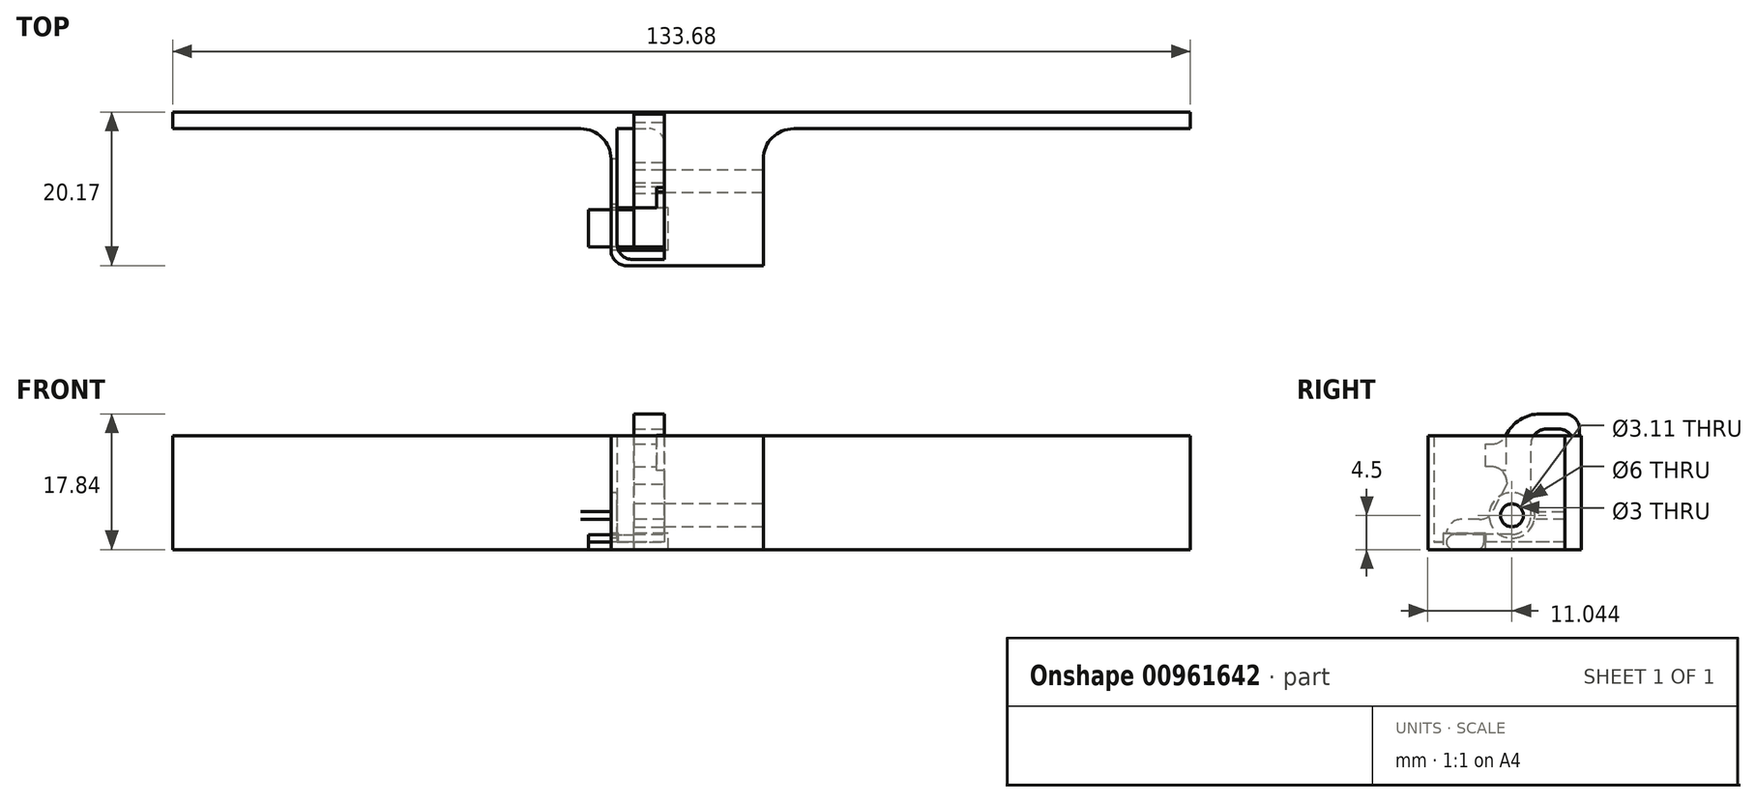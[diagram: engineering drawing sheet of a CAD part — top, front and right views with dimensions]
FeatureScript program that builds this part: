
annotation { "Feature Type Name" : "Feature", "Feature Type Description" : "" }
export const myFeature = defineFeature(function(context is Context, id is Id, definition is map)
    precondition{}
    {
        {
            var Q0;
            Q0=qCreatedBy(makeId("Top.planeOp"),FACE);
            var sketch = newSketch(context, id + "F0", { "sketchPlane" : qUnion([Q0])});
            skLineSegment(sketch, "E0.bottom", {"start": v(-38.38, 26.4) * mm, "end": v(95.3, 26.4) * mm});
            skLineSegment(sketch, "E0.top", {"start": v(-38.38, 24.23) * mm, "end": v(95.3, 24.23) * mm});
            skLineSegment(sketch, "E0.left", {"start": v(-38.38, 26.4) * mm, "end": v(-38.38, 24.23) * mm});
            skLineSegment(sketch, "E0.right", {"start": v(95.3, 26.4) * mm, "end": v(95.3, 24.23) * mm});
            skLineSegment(sketch, "E1.bottom", {"start": v(26.2, 24.23) * mm, "end": v(39.2, 24.23) * mm});
            skLineSegment(sketch, "E1.top", {"start": v(26.2, 6.23) * mm, "end": v(39.2, 6.23) * mm});
            skLineSegment(sketch, "E1.left", {"start": v(26.2, 24.23) * mm, "end": v(26.2, 6.23) * mm});
            skLineSegment(sketch, "E1.right", {"start": v(39.2, 24.23) * mm, "end": v(39.2, 6.23) * mm});
            skSolve(sketch);
        }
        {
            var Q0;
            Q0 = qSketchRegion(id + "F0", true);
            extrude(context, id + "F1", {"entities" : qUnion([Q0]), "depth" : 15 * mm, "offsetDistance" : 25 * mm});
        }
        {
            var Q0;
            Q0=makeQuery(id+"F1.opExtrude","CAP_FACE",FACE,{"disambiguationData":[OSD([sQuery(id+"F0.wireOp",EDGE,"E0.bottom"),sQuery(id+"F0.wireOp",EDGE,"E0.top"),sQuery(id+"F0.wireOp",EDGE,"E0.left"),sQuery(id+"F0.wireOp",EDGE,"E0.right"),sQuery(id+"F0.wireOp",EDGE,"E1.top"),sQuery(id+"F0.wireOp",EDGE,"E1.left"),sQuery(id+"F0.wireOp",EDGE,"E1.right")])],"isStart":true});
            var sketch = newSketch(context, id + "F2", { "sketchPlane" : qUnion([Q0])});
            skLineSegment(sketch, "E2.bottom", {"start": v(26.2, -6.23) * mm, "end": v(19.2, -6.23) * mm});
            skLineSegment(sketch, "E2.top", {"start": v(26.2, -25.17) * mm, "end": v(19.2, -25.17) * mm});
            skLineSegment(sketch, "E2.left", {"start": v(26.2, -6.23) * mm, "end": v(26.2, -25.17) * mm});
            skLineSegment(sketch, "E2.right", {"start": v(19.2, -6.23) * mm, "end": v(19.2, -25.17) * mm});
            skSolve(sketch);
        }
        {
            var Q0;
            {var subQ0=sQuery(id+"F2.wireOp",EDGE,"E2.bottom");Q0=makeQuery(id+"F2.imprint","IMPRINT",FACE,{"disambiguationData":[TD([[makeQuery(id+"F2.imprint","IMPRINT",EDGE,{"derivedFrom":subQ0}),1.0]])]});}
            extrude(context, id + "F3", {"entities" : qUnion([Q0]), "operationType" : NewBodyOperationType.ADD, "oppositeDirection" : true, "depth" : 1 * mm, "offsetDistance" : 25 * mm});
        }
        {
            var Q0;
            Q0=makeQuery(id+"F3.opExtrude","CAP_FACE",FACE,{"disambiguationData":[OSD([sQuery(id+"F0.wireOp",EDGE,"E0.top"),sQuery(id+"F2.wireOp",EDGE,"E2.bottom"),sQuery(id+"F2.wireOp",EDGE,"E2.left"),sQuery(id+"F2.wireOp",EDGE,"E2.right")])],"isStart":false});
            var sketch = newSketch(context, id + "F4", { "sketchPlane" : qUnion([Q0])});
            skLineSegment(sketch, "E3.bottom", {"start": v(19.2, 24.23) * mm, "end": v(20, 24.23) * mm});
            skLineSegment(sketch, "E3.top", {"start": v(19.2, 6.23) * mm, "end": v(20, 6.23) * mm});
            skLineSegment(sketch, "E3.left", {"start": v(19.2, 24.23) * mm, "end": v(19.2, 6.23) * mm});
            skLineSegment(sketch, "E3.right", {"start": v(20, 24.23) * mm, "end": v(20, 6.23) * mm});
            skLineSegment(sketch, "E4.bottom", {"start": v(20, 6.23) * mm, "end": v(26.2, 6.23) * mm});
            skLineSegment(sketch, "E4.top", {"start": v(20, 7.03) * mm, "end": v(26.2, 7.03) * mm});
            skLineSegment(sketch, "E4.left", {"start": v(20, 6.23) * mm, "end": v(20, 7.03) * mm});
            skLineSegment(sketch, "E4.right", {"start": v(26.2, 6.23) * mm, "end": v(26.2, 7.03) * mm});
            skSolve(sketch);
        }
        {
            var Q0;
            Q0=makeQuery(id+"F4.imprint","IMPRINT",FACE,{"disambiguationData":[TD([[makeQuery(id+"F4.imprint","IMPRINT",EDGE,{"derivedFrom":sQuery(id+"F4.wireOp",EDGE,"E3.bottom")}),-1.0]])]});
            var Q1;
            Q1=makeQuery(id+"F4.imprint","IMPRINT",FACE,{"disambiguationData":[TD([[makeQuery(id+"F4.imprint","IMPRINT",EDGE,{"derivedFrom":sQuery(id+"F4.wireOp",EDGE,"E4.bottom")}),-1.0]])]});
            extrude(context, id + "F5", {"entities" : qUnion([Q0, Q1]), "operationType" : NewBodyOperationType.ADD, "depth" : 14 * mm, "offsetDistance" : 25 * mm});
        }
        {
            var Q0;
            Q0=makeQuery(id+"F5.boolean.opBoolean","MERGE",EDGE,{"derivedFrom":[makeQuery(id+"F3.opExtrude","SWEPT_EDGE",EDGE,{"disambiguationData":[OSD([sQuery(id+"F2.wireOp",EDGE,"E2.bottom"),sQuery(id+"F2.wireOp",EDGE,"E2.right")])]}),makeQuery(id+"F5.opExtrude","SWEPT_EDGE",EDGE,{"disambiguationData":[OSD([sQuery(id+"F4.wireOp",EDGE,"E3.top"),sQuery(id+"F4.wireOp",EDGE,"E3.left")])]})]});
            var Q1;
            Q1=makeQuery(id+"F1.opExtrude","SWEPT_EDGE",EDGE,{"disambiguationData":[OSD([sQuery(id+"F0.wireOp",EDGE,"E0.top"),sQuery(id+"F0.wireOp",EDGE,"E1.bottom"),sQuery(id+"F0.wireOp",EDGE,"E1.left")])]});
            var Q2;
            Q2=makeQuery(id+"F5.opExtrude","SWEPT_EDGE",EDGE,{"disambiguationData":[OSD([sQuery(id+"F0.wireOp",EDGE,"E0.top"),sQuery(id+"F4.wireOp",EDGE,"E3.bottom"),sQuery(id+"F4.wireOp",EDGE,"E3.right")])]});
            var Q3;
            Q3=makeQuery(id+"F5.opExtrude","SWEPT_EDGE",EDGE,{"disambiguationData":[OSD([sQuery(id+"F4.wireOp",EDGE,"E3.right"),sQuery(id+"F4.wireOp",EDGE,"E4.top"),sQuery(id+"F4.wireOp",EDGE,"E4.left")])]});
            var Q4;
            Q4=makeQuery(id+"F5.opExtrude","SWEPT_EDGE",EDGE,{"disambiguationData":[OSD([sQuery(id+"F2.wireOp",EDGE,"E2.left"),sQuery(id+"F4.wireOp",EDGE,"E4.top"),sQuery(id+"F4.wireOp",EDGE,"E4.right")])]});
            fillet(context, id + "F6", {"entities" : qUnion([Q0, Q1, Q2, Q3, Q4]), "radius" : 2 * mm, "tangentPropagation" : true, "allowEdgeOverflow" : false});
        }
        {
            var Q0;
            Q0=makeQuery(id+"F5.boolean.opBoolean","MERGE",FACE,{"derivedFrom":[makeQuery(id+"F3.opExtrude","SWEPT_FACE",FACE,{"disambiguationData":[OSD([sQuery(id+"F2.wireOp",EDGE,"E2.right")])]}),makeQuery(id+"F5.opExtrude","SWEPT_FACE",FACE,{"disambiguationData":[OSD([sQuery(id+"F4.wireOp",EDGE,"E3.left")])]})]});
            var sketch = newSketch(context, id + "F7", { "sketchPlane" : qUnion([Q0])});
            skCircle(sketch, "E5", {"center": v(-17.27, 4.5) * mm, "radius": 3 * mm});
            skSolve(sketch);
        }
        {
            var Q0;
            Q0 = qSketchRegion(id + "F7", true);
            extrude(context, id + "F8", {"entities" : qUnion([Q0]), "operationType" : NewBodyOperationType.REMOVE, "oppositeDirection" : true, "depth" : 2 * mm, "offsetDistance" : 25 * mm});
        }
        {
            var Q0;
            Q0=makeQuery(id+"F1.opExtrude","SWEPT_FACE",FACE,{"disambiguationData":[OSD([sQuery(id+"F0.wireOp",EDGE,"E1.left")])]});
            var sketch = newSketch(context, id + "F9", { "sketchPlane" : qUnion([Q0])});
            skCircle(sketch, "E6", {"center": v(-17.27, 4.5) * mm, "radius": 1.5 * mm});
            skSolve(sketch);
        }
        {
            var Q0;
            Q0 = qSketchRegion(id + "F9", true);
            extrude(context, id + "F10", {"entities" : qUnion([Q0]), "operationType" : NewBodyOperationType.REMOVE, "oppositeDirection" : true, "depth" : 25 * mm, "offsetDistance" : 25 * mm});
        }
        {
            var Q0;
            Q0=makeQuery(id+"F1.opExtrude","SWEPT_EDGE",EDGE,{"disambiguationData":[OSD([sQuery(id+"F0.wireOp",EDGE,"E0.top"),sQuery(id+"F0.wireOp",EDGE,"E1.bottom"),sQuery(id+"F0.wireOp",EDGE,"E1.right")])]});
            var Q1;
            Q1=makeQuery(id+"F5.boolean.opBoolean","MERGE",EDGE,{"derivedFrom":[makeQuery(id+"F3.opExtrude","SWEPT_EDGE",EDGE,{"disambiguationData":[OSD([sQuery(id+"F0.wireOp",EDGE,"E0.top"),sQuery(id+"F2.wireOp",EDGE,"E2.right")])]}),makeQuery(id+"F5.opExtrude","SWEPT_EDGE",EDGE,{"disambiguationData":[OSD([sQuery(id+"F4.wireOp",EDGE,"E3.bottom"),sQuery(id+"F4.wireOp",EDGE,"E3.left")])]})]});
            fillet(context, id + "F11", {"entities" : qUnion([Q0, Q1]), "radius" : 4 * mm, "tangentPropagation" : true, "allowEdgeOverflow" : false});
        }
        {
            var Q0;
            Q0=makeQuery(id+"F1.opExtrude","SWEPT_FACE",FACE,{"disambiguationData":[OSD([sQuery(id+"F0.wireOp",EDGE,"E1.left")])]});
            var sketch = newSketch(context, id + "F12", { "sketchPlane" : qUnion([Q0])});
            skCircle(sketch, "E7", {"center": v(-17.27, 4.5) * mm, "radius": 1.55 * mm});
            skArc(sketch, "E8", {"start": v(-14.83, 3.98) * mm, "mid": v(-14.8, 4.83) * mm, "end": v(-15.05, 5.65) * mm});
            skLineSegment(sketch, "E9", {"start": v(-19.77, 4.52) * mm, "end": v(-19.77, 15.84) * mm});
            skLineSegment(sketch, "E10", {"start": v(-19.77, 15.84) * mm, "end": v(-25.1, 15.84) * mm});
            skLineSegment(sketch, "E11", {"start": v(-25.1, 15.84) * mm, "end": v(-25.1, 15) * mm});
            skLineSegment(sketch, "E12", {"start": v(-25.1, 15) * mm, "end": v(-26.15, 15) * mm});
            skLineSegment(sketch, "E13", {"start": v(-26.15, 15) * mm, "end": v(-26.15, 17.84) * mm});
            skLineSegment(sketch, "E14", {"start": v(-26.15, 17.84) * mm, "end": v(-16.7, 17.84) * mm});
            skLineSegment(sketch, "E15", {"start": v(-16.7, 17.84) * mm, "end": v(-16.7, 13.9) * mm});
            skLineSegment(sketch, "E16", {"start": v(-16.7, 13.9) * mm, "end": v(-13.85, 13.9) * mm});
            skLineSegment(sketch, "E17", {"start": v(-13.85, 13.9) * mm, "end": v(-13.85, 10.9) * mm});
            skLineSegment(sketch, "E18", {"start": v(-13.85, 10.9) * mm, "end": v(-16.6, 10.9) * mm});
            skLineSegment(sketch, "E19", {"start": v(-16.6, 10.9) * mm, "end": v(-16.6, 8.65) * mm});
            skLineSegment(sketch, "E20", {"start": v(-16.6, 8.65) * mm, "end": v(-15.05, 5.65) * mm});
            skLineSegment(sketch, "E21", {"start": v(-17.16, 2) * mm, "end": v(-13.6, 2) * mm});
            skLineSegment(sketch, "E22", {"start": v(-13.6, 2) * mm, "end": v(-13.6, 0) * mm});
            skLineSegment(sketch, "E23", {"start": v(-13.6, 0) * mm, "end": v(-8.67, 0) * mm});
            skLineSegment(sketch, "E24", {"start": v(-8.67, 0) * mm, "end": v(-8.67, 1.95) * mm});
            skLineSegment(sketch, "E25", {"start": v(-14.83, 3.98) * mm, "end": v(-8.63, 3.98) * mm});
            skLineSegment(sketch, "E26", {"start": v(-8.63, 3.98) * mm, "end": v(-8.67, 1.95) * mm});
            skArc(sketch, "E27.trimOffspring", {"start": v(-19.77, 4.52) * mm, "mid": v(-19, 2.7) * mm, "end": v(-17.16, 2) * mm});
            skSolve(sketch);
        }
        {
            var Q0;
            Q0 = qSketchRegion(id + "F12", true);
            extrude(context, id + "F13", {"entities" : qUnion([Q0]), "depth" : 4 * mm, "offsetDistance" : 25 * mm});
        }
        {
            var Q0;
            Q0=makeQuery(id+"F5.boolean.opBoolean","MERGE",FACE,{"derivedFrom":[makeQuery(id+"F3.opExtrude","SWEPT_FACE",FACE,{"disambiguationData":[OSD([sQuery(id+"F2.wireOp",EDGE,"E2.right")])]}),makeQuery(id+"F5.opExtrude","SWEPT_FACE",FACE,{"disambiguationData":[OSD([sQuery(id+"F4.wireOp",EDGE,"E3.left")])]})]});
            var sketch = newSketch(context, id + "F14", { "sketchPlane" : qUnion([Q0])});
            skLineSegment(sketch, "E28.bottom", {"start": v(-13.81, 0) * mm, "end": v(-8.23, 0) * mm});
            skLineSegment(sketch, "E28.top", {"start": v(-13.81, 2.14) * mm, "end": v(-8.23, 2.14) * mm});
            skLineSegment(sketch, "E28.left", {"start": v(-13.81, 0) * mm, "end": v(-13.81, 2.14) * mm});
            skLineSegment(sketch, "E28.right", {"start": v(-8.23, 0) * mm, "end": v(-8.23, 2.14) * mm});
            skSolve(sketch);
        }
        {
            var Q0;
            Q0 = qSketchRegion(id + "F14", true);
            extrude(context, id + "F15", {"entities" : qUnion([Q0]), "operationType" : NewBodyOperationType.REMOVE, "oppositeDirection" : true, "depth" : 7.5 * mm, "offsetDistance" : 25 * mm});
        }
        {
            var Q0;
            Q0=makeQuery(id+"F13.opExtrude","CAP_FACE",FACE,{"disambiguationData":[OSD([sQuery(id+"F12.wireOp",EDGE,"E7"),sQuery(id+"F12.wireOp",EDGE,"E8"),sQuery(id+"F12.wireOp",EDGE,"E9"),sQuery(id+"F12.wireOp",EDGE,"E10"),sQuery(id+"F12.wireOp",EDGE,"E11"),sQuery(id+"F12.wireOp",EDGE,"E12"),sQuery(id+"F12.wireOp",EDGE,"E13"),sQuery(id+"F12.wireOp",EDGE,"E14"),sQuery(id+"F12.wireOp",EDGE,"E15"),sQuery(id+"F12.wireOp",EDGE,"E16"),sQuery(id+"F12.wireOp",EDGE,"E17"),sQuery(id+"F12.wireOp",EDGE,"E18"),sQuery(id+"F12.wireOp",EDGE,"E19"),sQuery(id+"F12.wireOp",EDGE,"E20"),sQuery(id+"F12.wireOp",EDGE,"E21"),sQuery(id+"F12.wireOp",EDGE,"E22"),sQuery(id+"F12.wireOp",EDGE,"E23"),sQuery(id+"F12.wireOp",EDGE,"E24"),sQuery(id+"F12.wireOp",EDGE,"E25"),sQuery(id+"F12.wireOp",EDGE,"E26"),sQuery(id+"F12.wireOp",EDGE,"E27.trimOffspring")])],"isStart":false});
            var sketch = newSketch(context, id + "F16", { "sketchPlane" : qUnion([Q0])});
            skLineSegment(sketch, "E29.bottom", {"start": v(-13.6, 0) * mm, "end": v(-8.67, 0) * mm});
            skLineSegment(sketch, "E29.top", {"start": v(-13.6, 1.95) * mm, "end": v(-8.67, 1.95) * mm});
            skLineSegment(sketch, "E29.left", {"start": v(-13.6, 0) * mm, "end": v(-13.6, 1.95) * mm});
            skLineSegment(sketch, "E29.right", {"start": v(-8.67, 0) * mm, "end": v(-8.67, 1.95) * mm});
            skSolve(sketch);
        }
        {
            var Q0;
            Q0 = qSketchRegion(id + "F16", true);
            extrude(context, id + "F17", {"entities" : qUnion([Q0]), "operationType" : NewBodyOperationType.ADD, "depth" : 6 * mm, "offsetDistance" : 25 * mm});
        }
        {
            var Q0;
            Q0=makeQuery(id+"F13.opExtrude","SWEPT_EDGE",EDGE,{"disambiguationData":[OSD([sQuery(id+"F12.wireOp",EDGE,"E15"),sQuery(id+"F12.wireOp",EDGE,"E16")])]});
            var Q1;
            Q1=makeQuery(id+"F13.opExtrude","SWEPT_EDGE",EDGE,{"disambiguationData":[OSD([sQuery(id+"F12.wireOp",EDGE,"E18"),sQuery(id+"F12.wireOp",EDGE,"E19")])]});
            var Q2;
            Q2=makeQuery(id+"F13.opExtrude","SWEPT_EDGE",EDGE,{"disambiguationData":[OSD([sQuery(id+"F12.wireOp",EDGE,"E13"),sQuery(id+"F12.wireOp",EDGE,"E14")])]});
            var Q3;
            Q3=makeQuery(id+"F13.opExtrude","SWEPT_EDGE",EDGE,{"disambiguationData":[OSD([sQuery(id+"F12.wireOp",EDGE,"E8"),sQuery(id+"F12.wireOp",EDGE,"E25")])]});
            var Q4;
            Q4=makeQuery(id+"F13.opExtrude","SWEPT_EDGE",EDGE,{"disambiguationData":[OSD([sQuery(id+"F12.wireOp",EDGE,"E21"),sQuery(id+"F12.wireOp",EDGE,"E22")])]});
            var Q5;
            Q5=makeQuery(id+"F13.opExtrude","SWEPT_EDGE",EDGE,{"disambiguationData":[OSD([sQuery(id+"F12.wireOp",EDGE,"E10"),sQuery(id+"F12.wireOp",EDGE,"E11")])]});
            var Q6;
            Q6=makeQuery(id+"F13.opExtrude","SWEPT_EDGE",EDGE,{"disambiguationData":[OSD([sQuery(id+"F12.wireOp",EDGE,"E9"),sQuery(id+"F12.wireOp",EDGE,"E10")])]});
            var Q7;
            Q7=makeQuery(id+"F13.opExtrude","SWEPT_EDGE",EDGE,{"disambiguationData":[OSD([sQuery(id+"F12.wireOp",EDGE,"E25"),sQuery(id+"F12.wireOp",EDGE,"E26")])]});
            fillet(context, id + "F18", {"entities" : qUnion([Q0, Q1, Q2, Q3, Q4, Q5, Q6, Q7]), "radius" : 2 * mm, "tangentPropagation" : true, "allowEdgeOverflow" : false});
        }
        {
            var Q0;
            Q0=makeQuery(id+"F13.opExtrude","SWEPT_EDGE",EDGE,{"disambiguationData":[OSD([sQuery(id+"F12.wireOp",EDGE,"E14"),sQuery(id+"F12.wireOp",EDGE,"E15")])]});
            fillet(context, id + "F19", {"entities" : qUnion([Q0]), "radius" : 5 * mm, "tangentPropagation" : true, "allowEdgeOverflow" : false});
        }
        {
            var Q0;
            Q0=makeQuery(id+"F18.opFillet","BLEND_EDGE",EDGE,{"blendedFrom":[makeQuery(id+"F13.opExtrude","SWEPT_EDGE",EDGE,{"disambiguationData":[OSD([sQuery(id+"F12.wireOp",EDGE,"E21"),sQuery(id+"F12.wireOp",EDGE,"E22")])]}),makeQuery(id+"F17.opExtrude","SWEPT_FACE",FACE,{"disambiguationData":[OSD([sQuery(id+"F16.wireOp",EDGE,"E29.top")])]})],"blendedInto":[makeQuery(id+"F17.opExtrude","SWEPT_FACE",FACE,{"disambiguationData":[OSD([sQuery(id+"F16.wireOp",EDGE,"E29.top")])]})]});
            var Q1;
            {var subQ0=sQuery(id+"F12.wireOp",EDGE,"E22");Q1=makeQuery(id+"F18.opFillet","BLEND_EDGE",EDGE,{"blendedFrom":[makeQuery(id+"F13.opExtrude","SWEPT_EDGE",EDGE,{"disambiguationData":[OSD([sQuery(id+"F12.wireOp",EDGE,"E21"),subQ0])]}),makeQuery(id+"F17.boolean.opBoolean","MERGE",FACE,{"derivedFrom":[makeQuery(id+"F13.opExtrude","SWEPT_FACE",FACE,{"disambiguationData":[OSD([subQ0])]}),makeQuery(id+"F17.opExtrude","SWEPT_FACE",FACE,{"disambiguationData":[OSD([sQuery(id+"F16.wireOp",EDGE,"E29.left")])]})]})],"blendedInto":[makeQuery(id+"F17.boolean.opBoolean","MERGE",FACE,{"derivedFrom":[makeQuery(id+"F13.opExtrude","SWEPT_FACE",FACE,{"disambiguationData":[OSD([subQ0])]}),makeQuery(id+"F17.opExtrude","SWEPT_FACE",FACE,{"disambiguationData":[OSD([sQuery(id+"F16.wireOp",EDGE,"E29.left")])]})]})]});}
            var Q2;
            Q2=makeQuery(id+"F17.opExtrude","SWEPT_EDGE",EDGE,{"disambiguationData":[OSD([sQuery(id+"F12.wireOp",EDGE,"E26"),sQuery(id+"F16.wireOp",EDGE,"E29.top"),sQuery(id+"F16.wireOp",EDGE,"E29.right")])]});
            var Q3;
            Q3=makeQuery(id+"F17.boolean.opBoolean","MERGE",EDGE,{"derivedFrom":[makeQuery(id+"F13.opExtrude","SWEPT_EDGE",EDGE,{"disambiguationData":[OSD([sQuery(id+"F12.wireOp",EDGE,"E23"),sQuery(id+"F12.wireOp",EDGE,"E24")])]}),makeQuery(id+"F17.opExtrude","SWEPT_EDGE",EDGE,{"disambiguationData":[OSD([sQuery(id+"F16.wireOp",EDGE,"E29.bottom"),sQuery(id+"F16.wireOp",EDGE,"E29.right")])]})]});
            fillet(context, id + "F20", {"entities" : qUnion([Q0, Q1, Q2, Q3]), "radius" : 1 * mm, "tangentPropagation" : true, "allowEdgeOverflow" : false});
        }
        {
            var Q0;
            Q0=makeQuery(id+"F17.boolean.opBoolean","MERGE",EDGE,{"derivedFrom":[makeQuery(id+"F13.opExtrude","SWEPT_EDGE",EDGE,{"disambiguationData":[OSD([sQuery(id+"F12.wireOp",EDGE,"E22"),sQuery(id+"F12.wireOp",EDGE,"E23")])]}),makeQuery(id+"F17.opExtrude","SWEPT_EDGE",EDGE,{"disambiguationData":[OSD([sQuery(id+"F16.wireOp",EDGE,"E29.bottom"),sQuery(id+"F16.wireOp",EDGE,"E29.left")])]})]});
            fillet(context, id + "F21", {"entities" : qUnion([Q0]), "radius" : 1 * mm, "tangentPropagation" : true, "allowEdgeOverflow" : false});
        }
        {
            var Q0;
            Q0=makeQuery(id+"F13.opExtrude","CAP_FACE",FACE,{"disambiguationData":[OSD([sQuery(id+"F12.wireOp",EDGE,"E7"),sQuery(id+"F12.wireOp",EDGE,"E8"),sQuery(id+"F12.wireOp",EDGE,"E9"),sQuery(id+"F12.wireOp",EDGE,"E10"),sQuery(id+"F12.wireOp",EDGE,"E11"),sQuery(id+"F12.wireOp",EDGE,"E12"),sQuery(id+"F12.wireOp",EDGE,"E13"),sQuery(id+"F12.wireOp",EDGE,"E14"),sQuery(id+"F12.wireOp",EDGE,"E15"),sQuery(id+"F12.wireOp",EDGE,"E16"),sQuery(id+"F12.wireOp",EDGE,"E17"),sQuery(id+"F12.wireOp",EDGE,"E18"),sQuery(id+"F12.wireOp",EDGE,"E19"),sQuery(id+"F12.wireOp",EDGE,"E20"),sQuery(id+"F12.wireOp",EDGE,"E21"),sQuery(id+"F12.wireOp",EDGE,"E22"),sQuery(id+"F12.wireOp",EDGE,"E23"),sQuery(id+"F12.wireOp",EDGE,"E24"),sQuery(id+"F12.wireOp",EDGE,"E25"),sQuery(id+"F12.wireOp",EDGE,"E26"),sQuery(id+"F12.wireOp",EDGE,"E27.trimOffspring")])],"isStart":true});
            var sketch = newSketch(context, id + "F22", { "sketchPlane" : qUnion([Q0])});
            skLineSegment(sketch, "E30.bottom", {"start": v(16.5, 15.02) * mm, "end": v(9.65, 15.02) * mm});
            skLineSegment(sketch, "E30.top", {"start": v(16.5, 10.42) * mm, "end": v(9.65, 10.42) * mm});
            skLineSegment(sketch, "E30.left", {"start": v(16.5, 15.02) * mm, "end": v(16.5, 10.42) * mm});
            skLineSegment(sketch, "E30.right", {"start": v(9.65, 15.02) * mm, "end": v(9.65, 10.42) * mm});
            skSolve(sketch);
        }
        {
            var Q0;
            Q0 = qSketchRegion(id + "F22", true);
            extrude(context, id + "F23", {"entities" : qUnion([Q0]), "operationType" : NewBodyOperationType.REMOVE, "oppositeDirection" : true, "depth" : 1 * mm, "offsetDistance" : 25 * mm});
        }
    });
